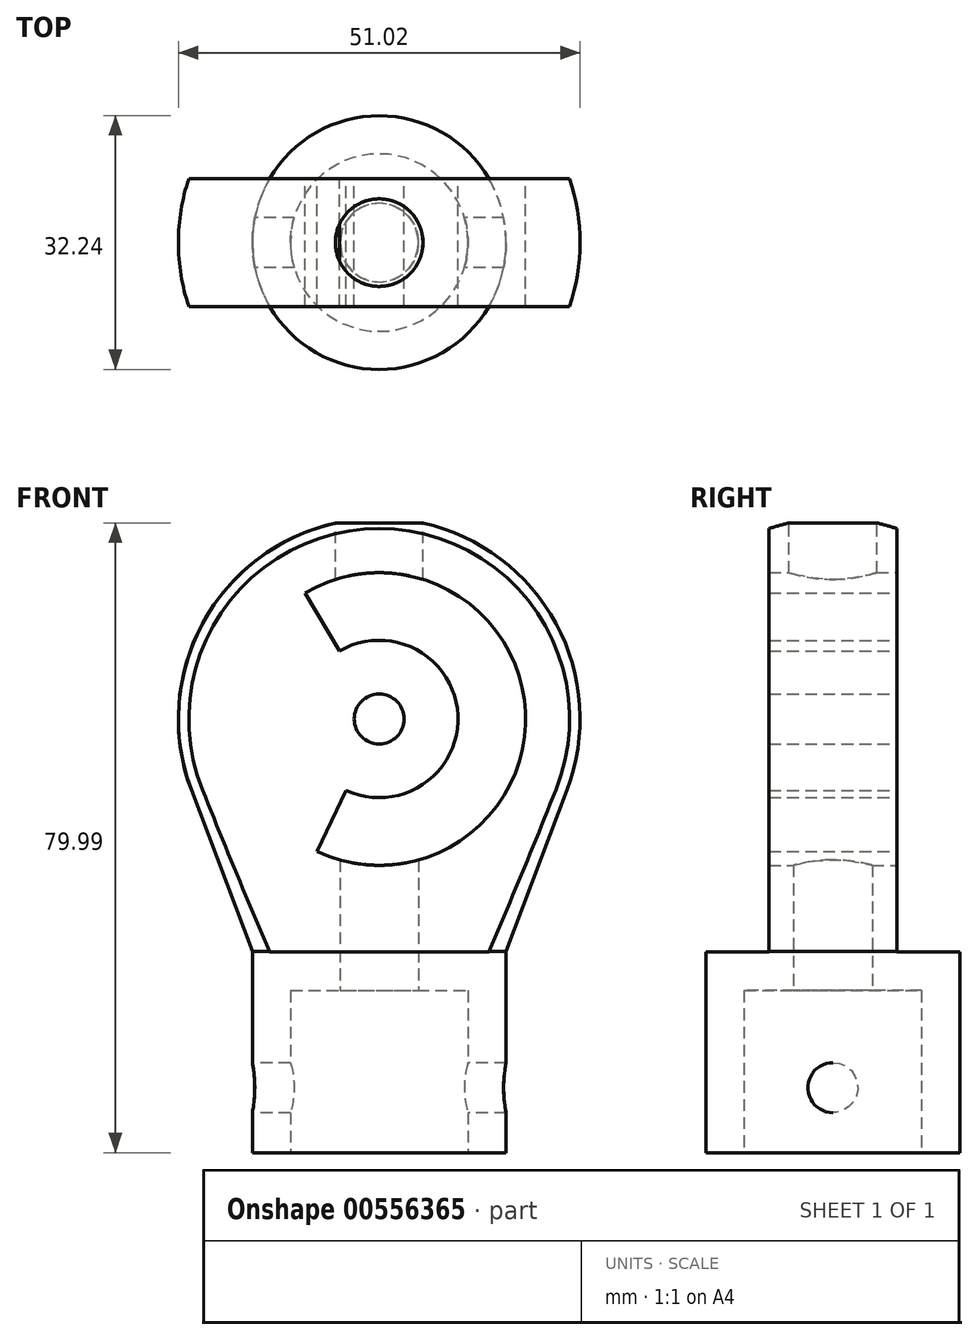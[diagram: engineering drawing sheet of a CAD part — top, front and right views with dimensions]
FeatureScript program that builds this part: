
annotation { "Feature Type Name" : "Feature", "Feature Type Description" : "" }
export const myFeature = defineFeature(function(context is Context, id is Id, definition is map)
    precondition{}
    {
        {
            var Q0;
            Q0=qCreatedBy(makeId("Front.planeOp"),FACE);
            var sketch = newSketch(context, id + "F0", { "sketchPlane" : qUnion([Q0])});
            skLineSegment(sketch, "E0.bottom", {"start": v(-16.12, -39.7) * mm, "end": v(13.25, -39.7) * mm});
            skLineSegment(sketch, "E0.top", {"start": v(-16.12, 11.48) * mm, "end": v(13.25, 11.48) * mm});
            skLineSegment(sketch, "E0.left", {"start": v(-16.12, -39.7) * mm, "end": v(-16.12, 11.48) * mm});
            skLineSegment(sketch, "E0.right", {"start": v(13.25, -39.7) * mm, "end": v(13.25, 11.48) * mm});
            skCircle(sketch, "E1", {"center": v(0, 15.38) * mm, "radius": 25.51 * mm});
            skLineSegment(sketch, "E2", {"start": v(-23.86, 6.36) * mm, "end": v(-16.12, -14.12) * mm});
            skLineSegment(sketch, "E3", {"start": v(22.55, 3.45) * mm, "end": v(13.25, -14.12) * mm});
            skLineSegment(sketch, "E4", {"start": v(0, 57.04) * mm, "end": v(0, -53.74) * mm, "construction": true});
            skLineSegment(sketch, "E5", {"start": v(0, -39.7) * mm, "end": v(0, 40.9) * mm});
            skSolve(sketch);
        }
        {
            var Q0;
            {var subQ4=sQuery(id+"F0.wireOp",EDGE,"E0.left");var subQ6=sQuery(id+"F0.wireOp",EDGE,"E0.top");var subQ7=makeQuery(id+"F0.imprint","INTERSECT",VERTEX,{"derivedFrom":[subQ6,subQ4]});Q0=makeQuery(id+"F0.imprint","IMPRINT",FACE,{"disambiguationData":[TD([[makeQuery(id+"F0.imprint","IMPRINT",EDGE,{"disambiguationData":[TD([[subQ7,-1.0]])],"derivedFrom":subQ6}),1.0]])]});}
            var Q1;
            {var subQ0=sQuery(id+"F0.wireOp",EDGE,"E0.left");var subQ1=sQuery(id+"F0.wireOp",EDGE,"E0.top");var subQ2=makeQuery(id+"F0.imprint","INTERSECT",VERTEX,{"derivedFrom":[subQ1,subQ0]});Q1=makeQuery(id+"F0.imprint","IMPRINT",FACE,{"disambiguationData":[TD([[makeQuery(id+"F0.imprint","IMPRINT",EDGE,{"disambiguationData":[TD([[subQ2,-1.0]])],"derivedFrom":subQ1}),-1.0]])]});}
            var Q2;
            {var subQ1=sQuery(id+"F0.wireOp",EDGE,"E0.left");var subQ5=sQuery(id+"F0.wireOp",EDGE,"E0.bottom");var subQ6=makeQuery(id+"F0.imprint","INTERSECT",VERTEX,{"derivedFrom":[subQ5,subQ1]});Q2=makeQuery(id+"F0.imprint","IMPRINT",FACE,{"disambiguationData":[TD([[makeQuery(id+"F0.imprint","IMPRINT",EDGE,{"disambiguationData":[TD([[subQ6,-1.0]])],"derivedFrom":subQ5}),1.0]])]});}
            var Q3;
            {var subQ0=sQuery(id+"F0.wireOp",EDGE,"E2");Q3=makeQuery(id+"F0.imprint","IMPRINT",FACE,{"disambiguationData":[TD([[makeQuery(id+"F0.imprint","IMPRINT",EDGE,{"derivedFrom":subQ0}),1.0]])]});}
            var Q4;
            Q4=sQuery(id+"F0.wireOp",EDGE,"E4");
            revolve(context, id + "F1", {"entities" : qUnion([Q0, Q1, Q2, Q3]), "axis" : qUnion([Q4]), "revolveType" : RevolveType.FULL});
        }
        {
            var Q0;
            Q0=qCreatedBy(makeId("Top.planeOp"),FACE);
            var sketch = newSketch(context, id + "F2", { "sketchPlane" : qUnion([Q0])});
            skLineSegment(sketch, "E6.bottom", {"start": v(-69.54, 49.43) * mm, "end": v(73.5, 49.43) * mm});
            skLineSegment(sketch, "E6.top", {"start": v(-69.54, 8.12) * mm, "end": v(73.5, 8.12) * mm});
            skLineSegment(sketch, "E6.left", {"start": v(-69.54, 49.43) * mm, "end": v(-69.54, 8.12) * mm});
            skLineSegment(sketch, "E6.right", {"start": v(73.5, 49.43) * mm, "end": v(73.5, 8.12) * mm});
            skLineSegment(sketch, "E7.MirrorCS", {"start": v(-69.54, -8.12) * mm, "end": v(73.5, -8.12) * mm});
            skLineSegment(sketch, "E8.MirrorCS", {"start": v(-69.54, -49.43) * mm, "end": v(-69.54, -8.12) * mm});
            skLineSegment(sketch, "E9.MirrorCS", {"start": v(-69.54, -49.43) * mm, "end": v(73.5, -49.43) * mm});
            skLineSegment(sketch, "E10.MirrorCS", {"start": v(73.5, -49.43) * mm, "end": v(73.5, -8.12) * mm});
            skSolve(sketch);
        }
        {
            var Q0;
            Q0 = qSketchRegion(id + "F2", true);
            extrude(context, id + "F3", {"entities" : qUnion([Q0]), "operationType" : NewBodyOperationType.REMOVE, "oppositeDirection" : true, "depth" : 14.2 * mm, "offsetDistance" : 25 * mm});
        }
        {
            var Q0;
            Q0 = qSketchRegion(id + "F2", true);
            extrude(context, id + "F4", {"entities" : qUnion([Q0]), "operationType" : NewBodyOperationType.REMOVE, "depth" : 45 * mm, "offsetDistance" : 25 * mm});
        }
        {
            var Q0;
            {var subQ0=sQuery(id+"F2.wireOp",EDGE,"E6.top");Q0=makeQuery(id+"F4.boolean.opBoolean","MERGE",FACE,{"derivedFrom":[makeQuery(id+"F3.boolean.opBoolean","COPY",FACE,{"derivedFrom":makeQuery(id+"F3.opExtrude","SWEPT_FACE",FACE,{"disambiguationData":[OSD([subQ0])]})}),makeQuery(id+"F4.opExtrude","SWEPT_FACE",FACE,{"disambiguationData":[OSD([subQ0])]})]});}
            var sketch = newSketch(context, id + "F5", { "sketchPlane" : qUnion([Q0])});
            skCircle(sketch, "E11", {"center": v(0, 15.38) * mm, "radius": 3.18 * mm});
            skCircle(sketch, "E12", {"center": v(0, 15.38) * mm, "radius": 10 * mm});
            skCircle(sketch, "E13", {"center": v(0, 15.38) * mm, "radius": 18.59 * mm});
            skLineSegment(sketch, "E14", {"start": v(4.24, 6.32) * mm, "end": v(7.87, -1.45) * mm});
            skLineSegment(sketch, "E15", {"start": v(5.07, 24) * mm, "end": v(9.42, 31.4) * mm});
            skSolve(sketch);
        }
        {
            var Q0;
            {var subQ0=sQuery(id+"F5.wireOp",EDGE,"E14");Q0=makeQuery(id+"F5.imprint","IMPRINT",FACE,{"disambiguationData":[TD([[makeQuery(id+"F5.imprint","IMPRINT",EDGE,{"derivedFrom":subQ0}),-1.0]])]});}
            var Q1;
            Q1=makeQuery(id+"F5.imprint","IMPRINT",FACE,{"disambiguationData":[TD([[makeQuery(id+"F5.imprint","IMPRINT",EDGE,{"derivedFrom":sQuery(id+"F5.wireOp",EDGE,"E11")}),1.0]])]});
            extrude(context, id + "F6", {"entities" : qUnion([Q0, Q1]), "operationType" : NewBodyOperationType.REMOVE, "oppositeDirection" : true, "depth" : 25 * mm, "offsetDistance" : 25 * mm});
        }
        {
            var Q0;
            Q0=makeQuery(id+"F1.opRevolve","SWEPT_FACE",FACE,{"disambiguationData":[OSD([sQuery(id+"F0.wireOp",EDGE,"E0.bottom")])]});
            var sketch = newSketch(context, id + "F7", { "sketchPlane" : qUnion([Q0])});
            skCircle(sketch, "E16", {"center": v(0, 0) * mm, "radius": 11.27 * mm});
            skCircle(sketch, "E17", {"center": v(0, 0) * mm, "radius": 5 * mm});
            skSolve(sketch);
        }
        {
            var Q0;
            Q0=makeQuery(id+"F7.imprint","IMPRINT",FACE,{"disambiguationData":[TD([[makeQuery(id+"F7.imprint","IMPRINT",EDGE,{"derivedFrom":sQuery(id+"F7.wireOp",EDGE,"E16")}),1.0]])]});
            extrude(context, id + "F8", {"entities" : qUnion([Q0]), "operationType" : NewBodyOperationType.REMOVE, "oppositeDirection" : true, "depth" : 20.6 * mm, "offsetDistance" : 25 * mm});
        }
        {
            var Q0;
            Q0=makeQuery(id+"F7.imprint","IMPRINT",FACE,{"disambiguationData":[TD([[makeQuery(id+"F7.imprint","IMPRINT",EDGE,{"derivedFrom":sQuery(id+"F7.wireOp",EDGE,"E17")}),1.0]])]});
            var Q1;
            Q1=makeQuery(id+"F6.boolean.opBoolean","COPY",FACE,{"derivedFrom":makeQuery(id+"F6.opExtrude","SWEPT_FACE",FACE,{"disambiguationData":[OSD([sQuery(id+"F5.wireOp",EDGE,"E13")])]})});
            extrude(context, id + "F9", {"entities" : qUnion([Q0]), "operationType" : NewBodyOperationType.REMOVE, "endBound" : BoundingType.UP_TO_SURFACE, "oppositeDirection" : true, "depth" : 25.6 * mm, "endBoundEntityFace" : qUnion([Q1]), "offsetDistance" : 25 * mm});
        }
        {
            var Q0;
            Q0=qCreatedBy(makeId("Top.planeOp"),FACE);
            cPlane(context, id + "F10", {"entities" : qUnion([Q0]), "cplaneType" : CPlaneType.OFFSET, "offset" : 41.8 * mm, "width" : 150 * mm, "height" : 150 * mm});
        }
        {
            var Q0;
            Q0=qCreatedBy(id+"F10.planeOp",FACE);
            var sketch = newSketch(context, id + "F11", { "sketchPlane" : qUnion([Q0])});
            skCircle(sketch, "E18", {"center": v(0, 0) * mm, "radius": 5.56 * mm});
            skSolve(sketch);
        }
        {
            var Q0;
            Q0 = qSketchRegion(id + "F11", true);
            extrude(context, id + "F12", {"entities" : qUnion([Q0]), "operationType" : NewBodyOperationType.REMOVE, "oppositeDirection" : true, "depth" : 13 * mm, "offsetDistance" : 25 * mm});
        }
        {
            var Q0;
            Q0=qCreatedBy(makeId("Right.planeOp"),FACE);
            var sketch = newSketch(context, id + "F13", { "sketchPlane" : qUnion([Q0])});
            skCircle(sketch, "E19", {"center": v(0, -31.45) * mm, "radius": 3.17 * mm});
            skSolve(sketch);
        }
        {
            var Q0;
            Q0 = qSketchRegion(id + "F13", true);
            extrude(context, id + "F14", {"entities" : qUnion([Q0]), "operationType" : NewBodyOperationType.REMOVE, "endBound" : BoundingType.THROUGH_ALL, "depth" : 25 * mm, "offsetDistance" : 25 * mm, "hasSecondDirection" : true, "secondDirectionOppositeDirection" : true, "secondDirectionDepth" : 25 * mm});
        }
    });
